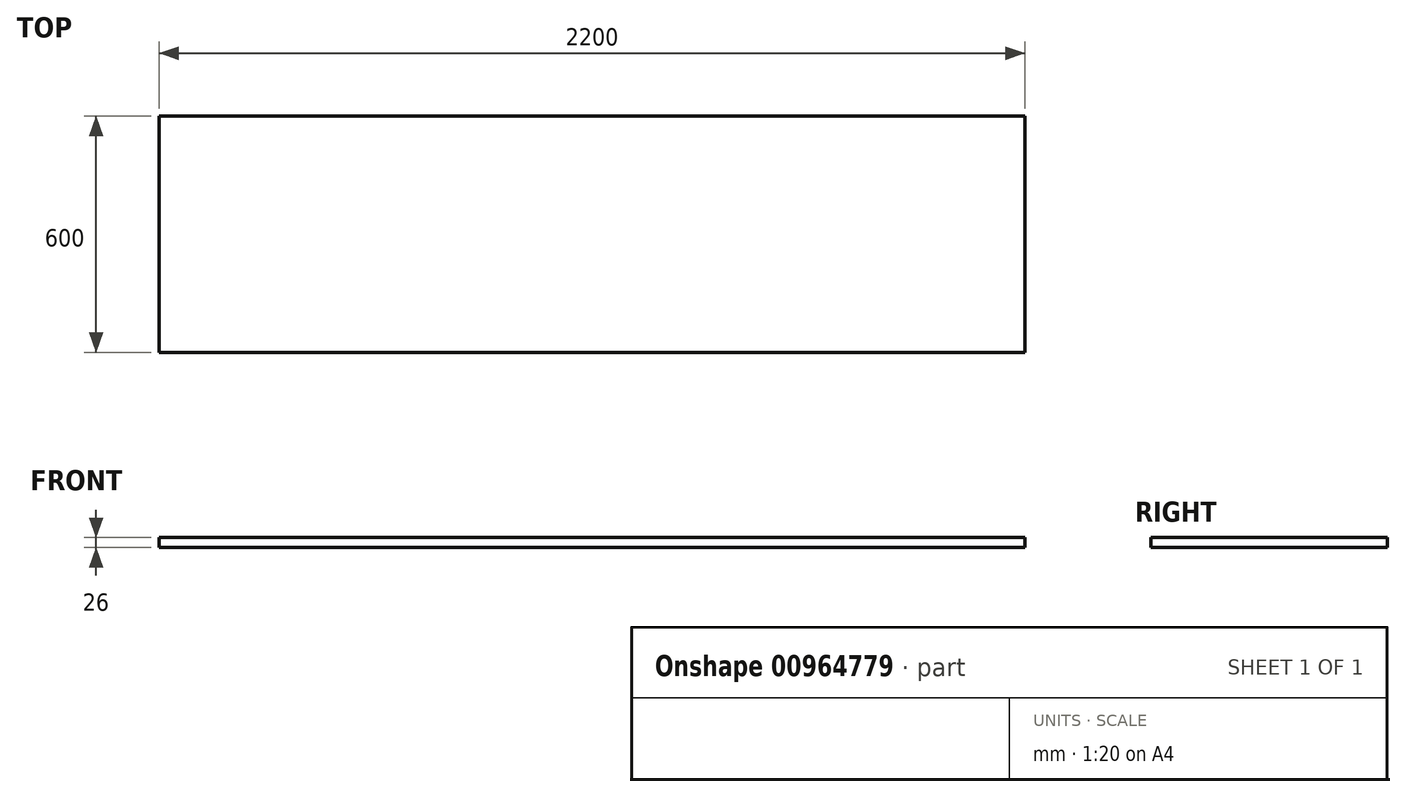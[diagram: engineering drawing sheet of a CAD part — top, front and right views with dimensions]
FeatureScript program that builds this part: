
annotation { "Feature Type Name" : "Feature", "Feature Type Description" : "" }
export const myFeature = defineFeature(function(context is Context, id is Id, definition is map)
    precondition{}
    {
        {
            var Q0;
            Q0=qCreatedBy(makeId("Top.planeOp"),FACE);
            var sketch = newSketch(context, id + "F0", { "sketchPlane" : qUnion([Q0])});
            skLineSegment(sketch, "E0.bottom", {"start": v(0, 0) * mm, "end": v(2200, 0) * mm});
            skLineSegment(sketch, "E0.top", {"start": v(0, -600) * mm, "end": v(2200, -600) * mm});
            skLineSegment(sketch, "E0.left", {"start": v(0, 0) * mm, "end": v(0, -600) * mm});
            skLineSegment(sketch, "E0.right", {"start": v(2200, 0) * mm, "end": v(2200, -600) * mm});
            skSolve(sketch);
        }
        {
            var Q0;
            Q0 = qSketchRegion(id + "F0", true);
            extrude(context, id + "F1", {"entities" : qUnion([Q0]), "depth" : 26 * mm, "offsetDistance" : 25 * mm});
        }
    });
